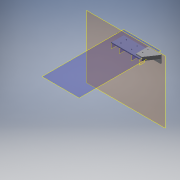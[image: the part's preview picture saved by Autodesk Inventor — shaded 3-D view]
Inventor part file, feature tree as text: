
AUTODESK INVENTOR PART (.ipt)
format: ipt  version: 2016 (Build 200138000, 138)  size: 247,296 bytes
history: native  units: in
note: dims shown in document units (in); Inventor stores cm internally (conversion verified against a paired STEP export)
features: extrude x10, sketch x10, reference x8, plane x7, projected_geometry x5, chamfer x1
ambient origin geometry x8: Origin, YZ Plane, XZ Plane, XY Plane, X Axis, Y Axis, Z Axis, Center Point
bodies: Solid1 (feature_tree)
feature tree (41):
  plane  "Work Plane1"
  extrude  "Extrusion1"  Depth=0.2in
  plane  "Work Plane2"
  extrude  "Extrusion2"  Depth=1.0in TaperAngle=0.0deg
  extrude  "Extrusion3"  Depth=2.5in
  sketch  "Sketch4"  dims[d10=0.2in d11=0.0in d12=0.2in d13=0.0in]
  plane  "Work Plane3"
  extrude  "Extrusion4"  Depth=0.2in TaperAngle=0.0deg
  extrude  "Extrusion5"  Depth=0.2in TaperAngle=0.0deg
  plane  "Work Plane4"
  extrude  "Extrusion6"  Depth=1.5625in
  plane  "Work Plane6"
  extrude  "Extrusion7"  Depth=0.2in TaperAngle=45.0deg
  extrude  "Extrusion8"  [1 undecoded]
  plane  "Work Plane7"
  extrude  "Extrusion9"  [1 undecoded]
  chamfer  "Chamfer1"  [1 undecoded]
  extrude  "Extrusion10"  [1 undecoded]
  sketch  "Sketch1"  dims[d0=0.2in d1=0.0in d2=0.75in]
  reference  "Reference1"
  reference  "Reference2"
  reference  "Reference3"
  reference  "Reference4"
  sketch  "Sketch2"  dims[d3=0.2in d4=0.0in d5=1.0in d6=0.0in]
  reference  "Reference5"
  sketch  "Sketch3"  dims[d7=0.2in d8=0.0in d9=2.5in]
  reference  "Reference6"
  projected_geometry  "Projected Loop1"
  sketch  "Sketch5"  dims[d14=1.625in d15=2.25in d16=0.2in d17=0.0in]
  projected_geometry  "Projected Loop2"
  reference  "Reference7"
  reference  "Reference8"
  sketch  "Sketch6"  dims[d18=0.2in d19=0.0in d20=1.5625in]
  plane  "Work Plane5"
  sketch  "Sketch7"  dims[d21=0.2in d22=0.0in d23=0.875in d24=0.125in d25=45.0deg]
  projected_geometry  "Projected Loop3"
  sketch  "Sketch8"  dims[d26=10.0in d27=0.0in]
  projected_geometry  "Projected Loop4"
  sketch  "Sketch9"
  projected_geometry  "Projected Loop5"
  sketch  "Sketch10"
note: 4 required parameter values undecoded (feature->parameter linkage not recoverable at this tier; creation-order binding heuristic only, values carry confidence <= 0.55)
